# Revit family: 482-vHH-M3-G321_NeWndw-005 5 panes
name_source: partatom
category: Windows
revit_build: Autodesk Revit Architecture 2012 (Build: 20110916_2132(x64)
units: mm (PartAtom-declared; Revit-internal decimal feet)

## types (1)
- 482-vHH-M3-G321_NeWndw-005 5 panes
    Default Sill Height = 1015 mm  [stored 3.33005 ft]
    Frame Colour (Ext) = <By Category>
    Frame Colour (Int) = <By Category>
    Glazing Type = Glass
    Height = 1810 mm  [stored 5.93832 ft]
    Rough Height = 1810 mm  [stored 5.93832 ft]
    Rough Width = 6610 mm  [stored 21.6864 ft]
    Wall Closure = By host
    Width = 6600 mm  [stored 21.6535 ft]
    p01 hinge left = No
    p01 hinge right = No
    p02 hinge left = No
    p02 hinge right = No
    p03 hinge left = No
    p03 hinge right = No
    p04 hinge left = No
    p04 hinge right = No
    p05 hinge left = No
    panel 01 width = 1320 mm  [stored 4.33071 ft]
    panel 02 width = 1320 mm  [stored 4.33071 ft]
    panel 03 width = 1320 mm  [stored 4.33071 ft]
    panel 04 width = 1320 mm  [stored 4.33071 ft]
    panel 05 width = 1320 mm  [stored 4.33071 ft]

note: [stored X ft] marks values corroborated as IEEE doubles in the binary element streams (Revit-internal decimal feet)

## geometry (parser evidence)
native form markers: Sweep x3
no freeform markers — native parametric forms only
